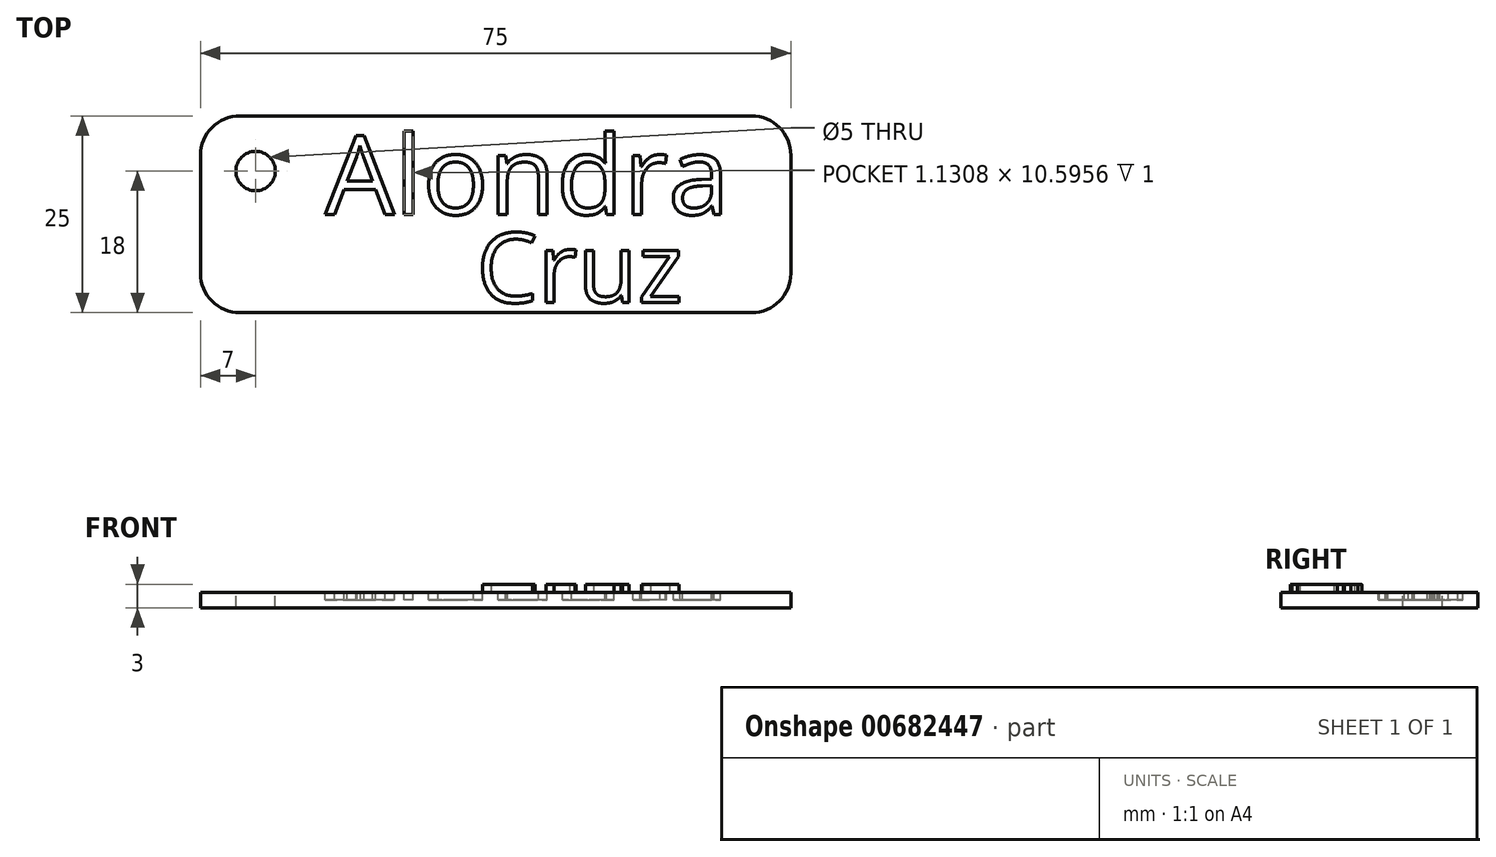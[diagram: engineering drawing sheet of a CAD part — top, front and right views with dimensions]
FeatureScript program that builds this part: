
annotation { "Feature Type Name" : "Feature", "Feature Type Description" : "" }
export const myFeature = defineFeature(function(context is Context, id is Id, definition is map)
    precondition{}
    {
        {
            var Q0;
            Q0=qCreatedBy(makeId("Top.planeOp"),FACE);
            var sketch = newSketch(context, id + "F0", { "sketchPlane" : qUnion([Q0])});
            skLineSegment(sketch, "E0.bottom", {"start": v(-32.5, 12.5) * mm, "end": v(32.5, 12.5) * mm});
            skLineSegment(sketch, "E0.top", {"start": v(-32.5, -12.5) * mm, "end": v(32.5, -12.5) * mm});
            skLineSegment(sketch, "E0.left", {"start": v(-37.5, 7.5) * mm, "end": v(-37.5, -7.5) * mm});
            skLineSegment(sketch, "E0.right", {"start": v(37.5, 7.5) * mm, "end": v(37.5, -7.5) * mm});
            skPoint(sketch, "E0.middle", {"position": v(0, 0) * mm});
            skPoint(sketch, "E1.visualSharp", {"position": v(-37.5, 12.5) * mm});
            skArc(sketch, "E1.filletArc", {"start": v(-32.5, 12.5) * mm, "mid": v(-36.04, 11.04) * mm, "end": v(-37.5, 7.5) * mm});
            skPoint(sketch, "E2.visualSharp", {"position": v(-37.5, -12.5) * mm});
            skArc(sketch, "E2.filletArc", {"start": v(-37.5, -7.5) * mm, "mid": v(-36.04, -11.04) * mm, "end": v(-32.5, -12.5) * mm});
            skPoint(sketch, "E3.visualSharp", {"position": v(37.5, -12.5) * mm});
            skArc(sketch, "E3.filletArc", {"start": v(32.5, -12.5) * mm, "mid": v(36.04, -11.04) * mm, "end": v(37.5, -7.5) * mm});
            skPoint(sketch, "E4.visualSharp", {"position": v(37.5, 12.5) * mm});
            skArc(sketch, "E4.filletArc", {"start": v(37.5, 7.5) * mm, "mid": v(36.04, 11.04) * mm, "end": v(32.5, 12.5) * mm});
            skSolve(sketch);
        }
        {
            var Q0;
            Q0=makeQuery(id+"F0.imprint","IMPRINT",FACE,{"disambiguationData":[TD([[makeQuery(id+"F0.imprint","IMPRINT",EDGE,{"derivedFrom":sQuery(id+"F0.wireOp",EDGE,"E0.bottom")}),-1.0]])]});
            extrude(context, id + "F1", {"entities" : qUnion([Q0]), "depth" : 2 * mm, "offsetDistance" : 25 * mm});
        }
        {
            var Q0;
            Q0=makeQuery(id+"F1.opExtrude","CAP_FACE",FACE,{"disambiguationData":[OSD([sQuery(id+"F0.wireOp",EDGE,"E0.bottom"),sQuery(id+"F0.wireOp",EDGE,"E0.top"),sQuery(id+"F0.wireOp",EDGE,"E0.left"),sQuery(id+"F0.wireOp",EDGE,"E0.right"),sQuery(id+"F0.wireOp",EDGE,"E1.filletArc"),sQuery(id+"F0.wireOp",EDGE,"E2.filletArc"),sQuery(id+"F0.wireOp",EDGE,"E3.filletArc"),sQuery(id+"F0.wireOp",EDGE,"E4.filletArc")])],"isStart":false});
            var sketch = newSketch(context, id + "F2", { "sketchPlane" : qUnion([Q0])});
            skPoint(sketch, "E5", {"position": v(-30.5, 5.5) * mm});
            skSolve(sketch);
        }
        {
            var Q0;
            Q0=sQuery(id+"F2.wireOp",VERTEX,"E5");
            var Q1;
            Q1=makeQuery(id+"F1.opExtrude","SWEPT_BODY",BODY,{"disambiguationData":[OSD([sQuery(id+"F0.wireOp",EDGE,"E0.bottom"),sQuery(id+"F0.wireOp",EDGE,"E0.top"),sQuery(id+"F0.wireOp",EDGE,"E0.left"),sQuery(id+"F0.wireOp",EDGE,"E0.right"),sQuery(id+"F0.wireOp",EDGE,"E1.filletArc"),sQuery(id+"F0.wireOp",EDGE,"E2.filletArc"),sQuery(id+"F0.wireOp",EDGE,"E3.filletArc"),sQuery(id+"F0.wireOp",EDGE,"E4.filletArc")])]});
            hole(context, id + "F3", {"style" : HoleStyle.SIMPLE, "endStyle" : HoleEndStyle.THROUGH, "holeDiameter" : 5 * mm, "majorDiameter" : 5 * mm, "isTappedThrough" : true, "tappedDepth" : 12 * mm, "tapClearance" : 3, "locations" : qUnion([Q0]), "scope" : qUnion([Q1])});
        }
        {
            var Q0;
            Q0=makeQuery(id+"F1.opExtrude","CAP_FACE",FACE,{"disambiguationData":[OSD([sQuery(id+"F0.wireOp",EDGE,"E0.bottom"),sQuery(id+"F0.wireOp",EDGE,"E0.top"),sQuery(id+"F0.wireOp",EDGE,"E0.left"),sQuery(id+"F0.wireOp",EDGE,"E0.right"),sQuery(id+"F0.wireOp",EDGE,"E1.filletArc"),sQuery(id+"F0.wireOp",EDGE,"E2.filletArc"),sQuery(id+"F0.wireOp",EDGE,"E3.filletArc"),sQuery(id+"F0.wireOp",EDGE,"E4.filletArc")])],"isStart":false});
            var sketch = newSketch(context, id + "F4", { "sketchPlane" : qUnion([Q0])});
            skText(sketch, "E6", { "text": "Alondra", "fontName": "OpenSans-Regular.ttf"});
            const initialGuessF4  = {"E6": [-0.02166, 0, 1, 0, 0.01004]};
            skSetInitialGuess(sketch, initialGuessF4);
            skSolve(sketch);
        }
        {
            var Q0;
            Q0 = qSketchRegion(id + "F4", true);
            extrude(context, id + "F5", {"entities" : qUnion([Q0]), "operationType" : NewBodyOperationType.REMOVE, "oppositeDirection" : true, "depth" : 1 * mm, "offsetDistance" : 25 * mm});
        }
        {
            var Q0;
            {var subQ0=sQuery(id+"F0.wireOp",EDGE,"E4.filletArc");var subQ1=sQuery(id+"F0.wireOp",EDGE,"E3.filletArc");var subQ2=sQuery(id+"F0.wireOp",EDGE,"E2.filletArc");var subQ3=sQuery(id+"F0.wireOp",EDGE,"E1.filletArc");var subQ4=sQuery(id+"F0.wireOp",EDGE,"E0.top");var subQ5=sQuery(id+"F0.wireOp",EDGE,"E0.bottom");var subQ6=sQuery(id+"F0.wireOp",EDGE,"E0.right");var subQ7=sQuery(id+"F0.wireOp",EDGE,"E0.left");Q0=makeQuery(id+"F5.boolean.opBoolean","SPLIT",FACE,{"disambiguationData":[TD([makeQuery(id+"F1.opExtrude","SWEPT_FACE",FACE,{"disambiguationData":[OSD([subQ5])]})])],"derivedFrom":makeQuery(id+"F1.opExtrude","CAP_FACE",FACE,{"disambiguationData":[OSD([subQ5,subQ4,subQ7,subQ6,subQ3,subQ2,subQ1,subQ0])],"isStart":false})});}
            var sketch = newSketch(context, id + "F6", { "sketchPlane" : qUnion([Q0])});
            skText(sketch, "E7", { "text": "Cruz", "fontName": "OpenSans-Regular.ttf"});
            const initialGuessF6  = {"E7": [-0.00244, -0.01119, 1, 0, 0.0089]};
            skSetInitialGuess(sketch, initialGuessF6);
            skSolve(sketch);
        }
        {
            var Q0;
            Q0 = qSketchRegion(id + "F6", true);
            extrude(context, id + "F7", {"entities" : qUnion([Q0]), "operationType" : NewBodyOperationType.ADD, "depth" : 1 * mm, "offsetDistance" : 25 * mm});
        }
    });
